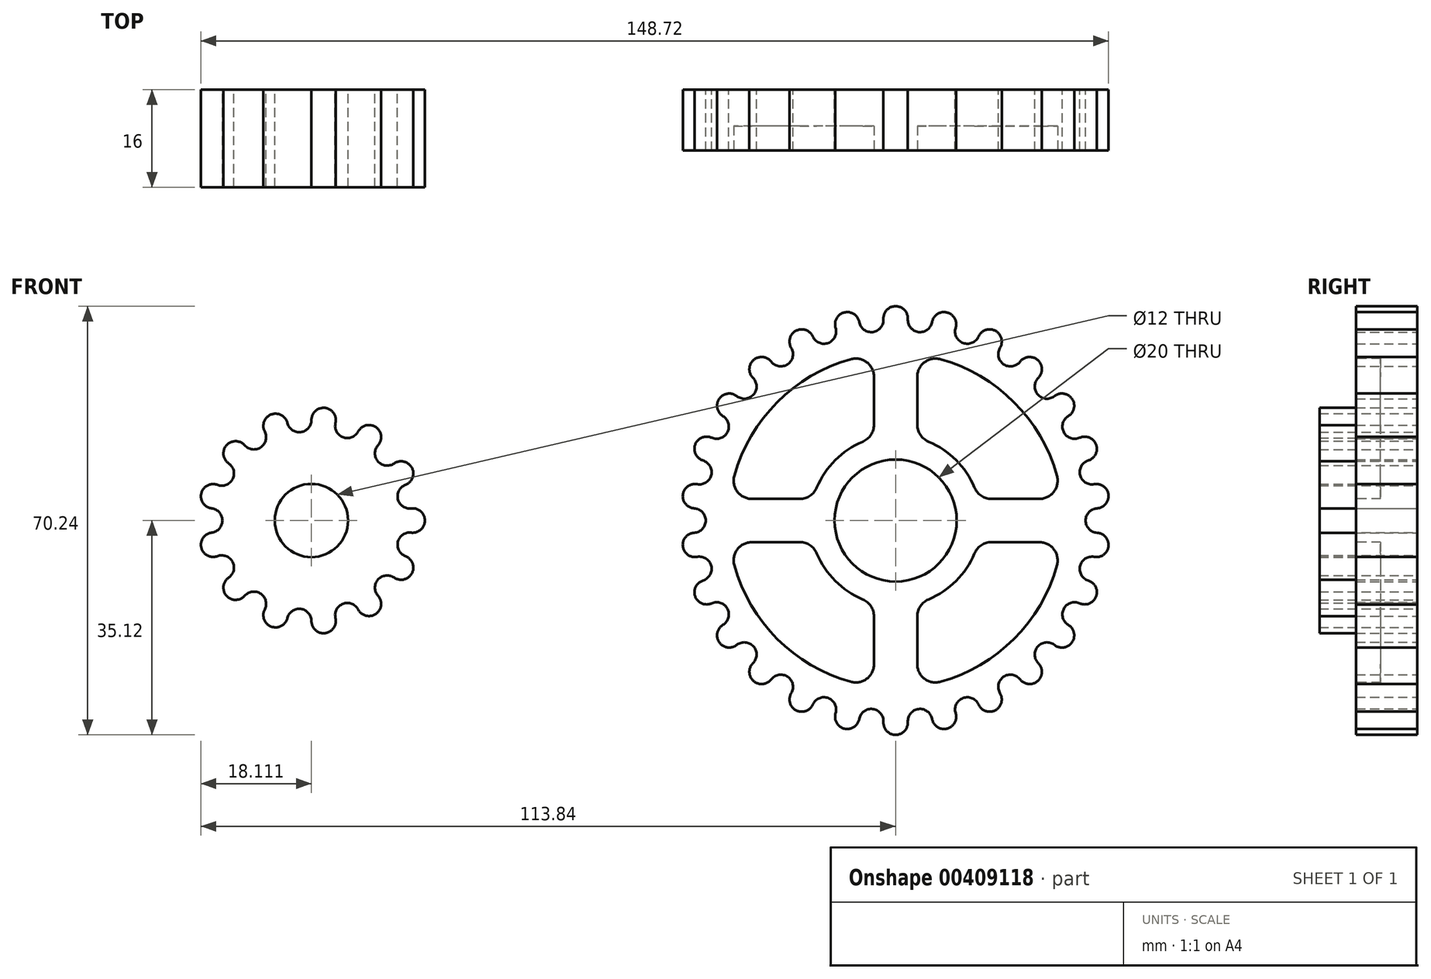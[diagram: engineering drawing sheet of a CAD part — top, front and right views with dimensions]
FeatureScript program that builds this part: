
annotation { "Feature Type Name" : "Feature", "Feature Type Description" : "" }
export const myFeature = defineFeature(function(context is Context, id is Id, definition is map)
    precondition{}
    {
        {
            var Q0;
            Q0=qCreatedBy(makeId("Front.planeOp"),FACE);
            var sketch = newSketch(context, id + "F0", { "sketchPlane" : qUnion([Q0])});
            skLineSegment(sketch, "E0", {"start": v(0, 0) * mm, "end": v(0, 49.58) * mm, "construction": true});
            skArc(sketch, "E1", {"start": v(0, 35.12) * mm, "mid": v(-1.46, 34.5) * mm, "end": v(-2, 33) * mm});
            skArc(sketch, "E2.1.0", {"start": v(-5.96, 32.52) * mm, "mid": v(-3.75, 30.9) * mm, "end": v(-2, 33) * mm});
            skPoint(sketch, "E2.center", {"position": v(0, 0) * mm});
            skLineSegment(sketch, "E3", {"start": v(0, 0) * mm, "end": v(-5.4, 44.45) * mm, "construction": true});
            skArc(sketch, "E4", {"start": v(-5.96, 32.52) * mm, "mid": v(-6.84, 33.84) * mm, "end": v(-8.4, 34.1) * mm});
            skLineSegment(sketch, "E5", {"start": v(0, 0) * mm, "end": v(-10.92, 44.32) * mm, "construction": true});
            skArc(sketch, "E6.1.0", {"start": v(-13.57, 30.15) * mm, "mid": v(-14.74, 31.22) * mm, "end": v(-16.32, 31.1) * mm});
            skArc(sketch, "E6.1.1", {"start": v(-13.57, 30.15) * mm, "mid": v(-11.04, 29.1) * mm, "end": v(-9.84, 31.57) * mm});
            skArc(sketch, "E6.1.2", {"start": v(-8.4, 34.1) * mm, "mid": v(-9.67, 33.14) * mm, "end": v(-9.84, 31.57) * mm});
            skArc(sketch, "E6.2.0", {"start": v(-20.4, 26.03) * mm, "mid": v(-21.78, 26.79) * mm, "end": v(-23.3, 26.3) * mm});
            skArc(sketch, "E6.2.1", {"start": v(-20.4, 26.03) * mm, "mid": v(-17.68, 25.61) * mm, "end": v(-17.1, 28.3) * mm});
            skArc(sketch, "E6.2.2", {"start": v(-16.32, 31.1) * mm, "mid": v(-17.32, 29.87) * mm, "end": v(-17.1, 28.3) * mm});
            skArc(sketch, "E6.3.0", {"start": v(-26.03, 20.4) * mm, "mid": v(-27.56, 20.8) * mm, "end": v(-28.9, 19.95) * mm});
            skArc(sketch, "E6.3.1", {"start": v(-26.03, 20.4) * mm, "mid": v(-23.3, 20.64) * mm, "end": v(-23.38, 23.38) * mm});
            skArc(sketch, "E6.3.2", {"start": v(-23.3, 26.3) * mm, "mid": v(-23.96, 24.85) * mm, "end": v(-23.38, 23.38) * mm});
            skArc(sketch, "E6.4.0", {"start": v(-30.15, 13.57) * mm, "mid": v(-31.74, 13.6) * mm, "end": v(-32.84, 12.46) * mm});
            skArc(sketch, "E6.4.1", {"start": v(-30.15, 13.57) * mm, "mid": v(-27.56, 14.46) * mm, "end": v(-28.3, 17.1) * mm});
            skArc(sketch, "E6.4.2", {"start": v(-28.9, 19.95) * mm, "mid": v(-29.22, 18.4) * mm, "end": v(-28.3, 17.1) * mm});
            skArc(sketch, "E6.5.0", {"start": v(-32.52, 5.96) * mm, "mid": v(-34.07, 5.6) * mm, "end": v(-34.87, 4.23) * mm});
            skArc(sketch, "E6.5.1", {"start": v(-32.52, 5.96) * mm, "mid": v(-30.22, 7.45) * mm, "end": v(-31.57, 9.84) * mm});
            skArc(sketch, "E6.5.2", {"start": v(-32.84, 12.46) * mm, "mid": v(-32.77, 10.87) * mm, "end": v(-31.57, 9.84) * mm});
            skArc(sketch, "E6.6.0", {"start": v(-33, -2) * mm, "mid": v(-34.42, -2.71) * mm, "end": v(-34.87, -4.23) * mm});
            skArc(sketch, "E6.6.1", {"start": v(-33, -2) * mm, "mid": v(-31.12, 0) * mm, "end": v(-33, 2) * mm});
            skArc(sketch, "E6.6.2", {"start": v(-34.87, 4.23) * mm, "mid": v(-34.42, 2.71) * mm, "end": v(-33, 2) * mm});
            skArc(sketch, "E6.7.0", {"start": v(-31.57, -9.84) * mm, "mid": v(-32.77, -10.87) * mm, "end": v(-32.84, -12.46) * mm});
            skArc(sketch, "E6.7.1", {"start": v(-31.57, -9.84) * mm, "mid": v(-30.22, -7.45) * mm, "end": v(-32.52, -5.96) * mm});
            skArc(sketch, "E6.7.2", {"start": v(-34.87, -4.23) * mm, "mid": v(-34.07, -5.6) * mm, "end": v(-32.52, -5.96) * mm});
            skArc(sketch, "E6.8.0", {"start": v(-28.3, -17.1) * mm, "mid": v(-29.22, -18.4) * mm, "end": v(-28.9, -19.95) * mm});
            skArc(sketch, "E6.8.1", {"start": v(-28.3, -17.1) * mm, "mid": v(-27.56, -14.46) * mm, "end": v(-30.15, -13.57) * mm});
            skArc(sketch, "E6.8.2", {"start": v(-32.84, -12.46) * mm, "mid": v(-31.74, -13.6) * mm, "end": v(-30.15, -13.57) * mm});
            skArc(sketch, "E6.9.0", {"start": v(-23.38, -23.38) * mm, "mid": v(-23.96, -24.85) * mm, "end": v(-23.3, -26.3) * mm});
            skArc(sketch, "E6.9.1", {"start": v(-23.38, -23.38) * mm, "mid": v(-23.3, -20.64) * mm, "end": v(-26.03, -20.4) * mm});
            skArc(sketch, "E6.9.2", {"start": v(-28.9, -19.95) * mm, "mid": v(-27.56, -20.8) * mm, "end": v(-26.03, -20.4) * mm});
            skArc(sketch, "E6.10.0", {"start": v(-17.1, -28.3) * mm, "mid": v(-17.32, -29.87) * mm, "end": v(-16.32, -31.1) * mm});
            skArc(sketch, "E6.10.1", {"start": v(-17.1, -28.3) * mm, "mid": v(-17.68, -25.61) * mm, "end": v(-20.4, -26.03) * mm});
            skArc(sketch, "E6.10.2", {"start": v(-23.3, -26.3) * mm, "mid": v(-21.78, -26.79) * mm, "end": v(-20.4, -26.03) * mm});
            skArc(sketch, "E6.11.0", {"start": v(-9.84, -31.57) * mm, "mid": v(-9.67, -33.14) * mm, "end": v(-8.4, -34.1) * mm});
            skArc(sketch, "E6.11.1", {"start": v(-9.84, -31.57) * mm, "mid": v(-11.04, -29.1) * mm, "end": v(-13.57, -30.15) * mm});
            skArc(sketch, "E6.11.2", {"start": v(-16.32, -31.1) * mm, "mid": v(-14.74, -31.22) * mm, "end": v(-13.57, -30.15) * mm});
            skArc(sketch, "E6.12.0", {"start": v(-2, -33) * mm, "mid": v(-1.46, -34.5) * mm, "end": v(0, -35.12) * mm});
            skArc(sketch, "E6.12.1", {"start": v(-2, -33) * mm, "mid": v(-3.75, -30.9) * mm, "end": v(-5.96, -32.52) * mm});
            skArc(sketch, "E6.12.2", {"start": v(-8.4, -34.1) * mm, "mid": v(-6.84, -33.84) * mm, "end": v(-5.96, -32.52) * mm});
            skArc(sketch, "E6.13.0", {"start": v(5.96, -32.52) * mm, "mid": v(6.84, -33.84) * mm, "end": v(8.4, -34.1) * mm});
            skArc(sketch, "E6.13.1", {"start": v(5.96, -32.52) * mm, "mid": v(3.75, -30.9) * mm, "end": v(2, -33) * mm});
            skArc(sketch, "E6.13.2", {"start": v(0, -35.12) * mm, "mid": v(1.46, -34.5) * mm, "end": v(2, -33) * mm});
            skArc(sketch, "E6.14.0", {"start": v(13.57, -30.15) * mm, "mid": v(14.74, -31.22) * mm, "end": v(16.32, -31.1) * mm});
            skArc(sketch, "E6.14.1", {"start": v(13.57, -30.15) * mm, "mid": v(11.04, -29.1) * mm, "end": v(9.84, -31.57) * mm});
            skArc(sketch, "E6.14.2", {"start": v(8.4, -34.1) * mm, "mid": v(9.67, -33.14) * mm, "end": v(9.84, -31.57) * mm});
            skArc(sketch, "E6.15.0", {"start": v(20.4, -26.03) * mm, "mid": v(21.78, -26.79) * mm, "end": v(23.3, -26.3) * mm});
            skArc(sketch, "E6.15.1", {"start": v(20.4, -26.03) * mm, "mid": v(17.68, -25.61) * mm, "end": v(17.1, -28.3) * mm});
            skArc(sketch, "E6.15.2", {"start": v(16.32, -31.1) * mm, "mid": v(17.32, -29.87) * mm, "end": v(17.1, -28.3) * mm});
            skArc(sketch, "E6.16.0", {"start": v(26.03, -20.4) * mm, "mid": v(27.56, -20.8) * mm, "end": v(28.9, -19.95) * mm});
            skArc(sketch, "E6.16.1", {"start": v(26.03, -20.4) * mm, "mid": v(23.3, -20.64) * mm, "end": v(23.38, -23.38) * mm});
            skArc(sketch, "E6.16.2", {"start": v(23.3, -26.3) * mm, "mid": v(23.96, -24.85) * mm, "end": v(23.38, -23.38) * mm});
            skArc(sketch, "E6.17.0", {"start": v(30.15, -13.57) * mm, "mid": v(31.74, -13.6) * mm, "end": v(32.84, -12.46) * mm});
            skArc(sketch, "E6.17.1", {"start": v(30.15, -13.57) * mm, "mid": v(27.56, -14.46) * mm, "end": v(28.3, -17.1) * mm});
            skArc(sketch, "E6.17.2", {"start": v(28.9, -19.95) * mm, "mid": v(29.22, -18.4) * mm, "end": v(28.3, -17.1) * mm});
            skArc(sketch, "E6.18.0", {"start": v(32.52, -5.96) * mm, "mid": v(34.07, -5.6) * mm, "end": v(34.87, -4.23) * mm});
            skArc(sketch, "E6.18.1", {"start": v(32.52, -5.96) * mm, "mid": v(30.22, -7.45) * mm, "end": v(31.57, -9.84) * mm});
            skArc(sketch, "E6.18.2", {"start": v(32.84, -12.46) * mm, "mid": v(32.77, -10.87) * mm, "end": v(31.57, -9.84) * mm});
            skArc(sketch, "E6.19.0", {"start": v(33, 2) * mm, "mid": v(34.42, 2.71) * mm, "end": v(34.87, 4.23) * mm});
            skArc(sketch, "E6.19.1", {"start": v(33, 2) * mm, "mid": v(31.12, 0) * mm, "end": v(33, -2) * mm});
            skArc(sketch, "E6.19.2", {"start": v(34.87, -4.23) * mm, "mid": v(34.42, -2.71) * mm, "end": v(33, -2) * mm});
            skArc(sketch, "E6.20.0", {"start": v(31.57, 9.84) * mm, "mid": v(32.77, 10.87) * mm, "end": v(32.84, 12.46) * mm});
            skArc(sketch, "E6.20.1", {"start": v(31.57, 9.84) * mm, "mid": v(30.22, 7.45) * mm, "end": v(32.52, 5.96) * mm});
            skArc(sketch, "E6.20.2", {"start": v(34.87, 4.23) * mm, "mid": v(34.07, 5.6) * mm, "end": v(32.52, 5.96) * mm});
            skArc(sketch, "E6.21.0", {"start": v(28.3, 17.1) * mm, "mid": v(29.22, 18.4) * mm, "end": v(28.9, 19.95) * mm});
            skArc(sketch, "E6.21.1", {"start": v(28.3, 17.1) * mm, "mid": v(27.56, 14.46) * mm, "end": v(30.15, 13.57) * mm});
            skArc(sketch, "E6.21.2", {"start": v(32.84, 12.46) * mm, "mid": v(31.74, 13.6) * mm, "end": v(30.15, 13.57) * mm});
            skArc(sketch, "E6.22.0", {"start": v(23.38, 23.38) * mm, "mid": v(23.96, 24.85) * mm, "end": v(23.3, 26.3) * mm});
            skArc(sketch, "E6.22.1", {"start": v(23.38, 23.38) * mm, "mid": v(23.3, 20.64) * mm, "end": v(26.03, 20.4) * mm});
            skArc(sketch, "E6.22.2", {"start": v(28.9, 19.95) * mm, "mid": v(27.56, 20.8) * mm, "end": v(26.03, 20.4) * mm});
            skArc(sketch, "E6.23.0", {"start": v(17.1, 28.3) * mm, "mid": v(17.32, 29.87) * mm, "end": v(16.32, 31.1) * mm});
            skArc(sketch, "E6.23.1", {"start": v(17.1, 28.3) * mm, "mid": v(17.68, 25.61) * mm, "end": v(20.4, 26.03) * mm});
            skArc(sketch, "E6.23.2", {"start": v(23.3, 26.3) * mm, "mid": v(21.78, 26.79) * mm, "end": v(20.4, 26.03) * mm});
            skArc(sketch, "E6.24.0", {"start": v(9.84, 31.57) * mm, "mid": v(9.67, 33.14) * mm, "end": v(8.4, 34.1) * mm});
            skArc(sketch, "E6.24.1", {"start": v(9.84, 31.57) * mm, "mid": v(11.04, 29.1) * mm, "end": v(13.57, 30.15) * mm});
            skArc(sketch, "E6.24.2", {"start": v(16.32, 31.1) * mm, "mid": v(14.74, 31.22) * mm, "end": v(13.57, 30.15) * mm});
            skArc(sketch, "E6.25.0", {"start": v(2, 33) * mm, "mid": v(1.46, 34.5) * mm, "end": v(0, 35.12) * mm});
            skArc(sketch, "E6.25.1", {"start": v(2, 33) * mm, "mid": v(3.75, 30.9) * mm, "end": v(5.96, 32.52) * mm});
            skArc(sketch, "E6.25.2", {"start": v(8.4, 34.1) * mm, "mid": v(6.84, 33.84) * mm, "end": v(5.96, 32.52) * mm});
            skCircle(sketch, "E7", {"center": v(0, 0) * mm, "radius": 10 * mm});
            skLineSegment(sketch, "E8", {"start": v(-95.73, 0) * mm, "end": v(-52.5, 0) * mm, "construction": true});
            skArc(sketch, "E9", {"start": v(-79.38, -1.99) * mm, "mid": v(-77.14, 0) * mm, "end": v(-79.38, 1.99) * mm});
            skArc(sketch, "E10.1.0", {"start": v(-81.56, 3.5) * mm, "mid": v(-80.75, 2.32) * mm, "end": v(-79.38, 1.99) * mm});
            skArc(sketch, "E10.25.0", {"start": v(-79.38, -1.99) * mm, "mid": v(-80.75, -2.32) * mm, "end": v(-81.56, -3.5) * mm});
            skPoint(sketch, "E10.center", {"position": v(-95.73, 0) * mm});
            skLineSegment(sketch, "E11", {"start": v(-95.73, 0) * mm, "end": v(-68.7, 6.66) * mm, "construction": true});
            skLineSegment(sketch, "E12", {"start": v(-95.73, 0) * mm, "end": v(-75.32, -5.03) * mm, "construction": true});
            skArc(sketch, "E13.1.0", {"start": v(-84.8, 9.68) * mm, "mid": v(-83.55, 9.02) * mm, "end": v(-82.17, 9.36) * mm});
            skArc(sketch, "E13.1.1", {"start": v(-80.33, 5.84) * mm, "mid": v(-79.27, 8.64) * mm, "end": v(-82.17, 9.36) * mm});
            skArc(sketch, "E13.1.2", {"start": v(-80.33, 5.84) * mm, "mid": v(-81.39, 4.9) * mm, "end": v(-81.56, 3.5) * mm});
            skArc(sketch, "E13.2.0", {"start": v(-90.55, 13.64) * mm, "mid": v(-89.14, 13.64) * mm, "end": v(-88.07, 14.58) * mm});
            skArc(sketch, "E13.2.1", {"start": v(-84.8, 12.33) * mm, "mid": v(-85.17, 15.3) * mm, "end": v(-88.07, 14.58) * mm});
            skArc(sketch, "E13.2.2", {"start": v(-84.8, 12.33) * mm, "mid": v(-85.3, 11) * mm, "end": v(-84.8, 9.68) * mm});
            skArc(sketch, "E14.2.3.0", {"start": v(-97.49, 14.49) * mm, "mid": v(-96.23, 15.15) * mm, "end": v(-95.73, 16.47) * mm});
            skArc(sketch, "E14.4.3.0", {"start": v(-91.79, 16) * mm, "mid": v(-93.49, 18.46) * mm, "end": v(-95.73, 16.47) * mm});
            skArc(sketch, "E14.8.3.0", {"start": v(-91.79, 16) * mm, "mid": v(-91.62, 14.58) * mm, "end": v(-90.55, 13.64) * mm});
            skArc(sketch, "E14.2.4.0", {"start": v(-104.02, 12) * mm, "mid": v(-103.21, 13.18) * mm, "end": v(-103.38, 14.58) * mm});
            skArc(sketch, "E14.4.4.0", {"start": v(-99.67, 16) * mm, "mid": v(-102.32, 17.38) * mm, "end": v(-103.38, 14.58) * mm});
            skArc(sketch, "E14.8.4.0", {"start": v(-99.67, 16) * mm, "mid": v(-98.86, 14.83) * mm, "end": v(-97.49, 14.49) * mm});
            skArc(sketch, "E14.2.5.0", {"start": v(-108.65, 6.78) * mm, "mid": v(-108.48, 8.19) * mm, "end": v(-109.28, 9.36) * mm});
            skArc(sketch, "E14.4.5.0", {"start": v(-106.65, 12.33) * mm, "mid": v(-109.65, 12.33) * mm, "end": v(-109.28, 9.36) * mm});
            skArc(sketch, "E14.8.5.0", {"start": v(-106.65, 12.33) * mm, "mid": v(-105.4, 11.67) * mm, "end": v(-104.02, 12) * mm});
            skArc(sketch, "E14.2.6.0", {"start": v(-110.32, 0) * mm, "mid": v(-110.82, 1.33) * mm, "end": v(-112.08, 1.99) * mm});
            skArc(sketch, "E14.4.6.0", {"start": v(-111.13, 5.84) * mm, "mid": v(-113.78, 4.45) * mm, "end": v(-112.08, 1.99) * mm});
            skArc(sketch, "E14.8.6.0", {"start": v(-111.13, 5.84) * mm, "mid": v(-109.71, 5.84) * mm, "end": v(-108.65, 6.78) * mm});
            skArc(sketch, "E14.2.7.0", {"start": v(-108.65, -6.78) * mm, "mid": v(-109.71, -5.84) * mm, "end": v(-111.13, -5.84) * mm});
            skArc(sketch, "E14.4.7.0", {"start": v(-112.08, -1.99) * mm, "mid": v(-113.78, -4.45) * mm, "end": v(-111.13, -5.84) * mm});
            skArc(sketch, "E14.8.7.0", {"start": v(-112.08, -1.99) * mm, "mid": v(-110.82, -1.33) * mm, "end": v(-110.32, 0) * mm});
            skArc(sketch, "E14.2.8.0", {"start": v(-104.02, -12) * mm, "mid": v(-105.4, -11.67) * mm, "end": v(-106.65, -12.33) * mm});
            skArc(sketch, "E14.4.8.0", {"start": v(-109.28, -9.36) * mm, "mid": v(-109.65, -12.33) * mm, "end": v(-106.65, -12.33) * mm});
            skArc(sketch, "E14.8.8.0", {"start": v(-109.28, -9.36) * mm, "mid": v(-108.48, -8.19) * mm, "end": v(-108.65, -6.78) * mm});
            skArc(sketch, "E14.2.9.0", {"start": v(-97.49, -14.49) * mm, "mid": v(-98.86, -14.83) * mm, "end": v(-99.67, -16) * mm});
            skArc(sketch, "E14.4.9.0", {"start": v(-103.38, -14.58) * mm, "mid": v(-102.32, -17.38) * mm, "end": v(-99.67, -16) * mm});
            skArc(sketch, "E14.8.9.0", {"start": v(-103.38, -14.58) * mm, "mid": v(-103.21, -13.18) * mm, "end": v(-104.02, -12) * mm});
            skArc(sketch, "E14.2.10.0", {"start": v(-90.55, -13.64) * mm, "mid": v(-91.62, -14.58) * mm, "end": v(-91.79, -16) * mm});
            skArc(sketch, "E14.4.10.0", {"start": v(-95.73, -16.47) * mm, "mid": v(-93.49, -18.46) * mm, "end": v(-91.79, -16) * mm});
            skArc(sketch, "E14.8.10.0", {"start": v(-95.73, -16.47) * mm, "mid": v(-96.23, -15.15) * mm, "end": v(-97.49, -14.49) * mm});
            skArc(sketch, "E14.2.11.0", {"start": v(-84.8, -9.68) * mm, "mid": v(-85.3, -11) * mm, "end": v(-84.8, -12.33) * mm});
            skArc(sketch, "E14.4.11.0", {"start": v(-88.07, -14.58) * mm, "mid": v(-85.17, -15.3) * mm, "end": v(-84.8, -12.33) * mm});
            skArc(sketch, "E14.8.11.0", {"start": v(-88.07, -14.58) * mm, "mid": v(-89.14, -13.64) * mm, "end": v(-90.55, -13.64) * mm});
            skArc(sketch, "E14.2.12.0", {"start": v(-81.56, -3.5) * mm, "mid": v(-81.39, -4.9) * mm, "end": v(-80.33, -5.84) * mm});
            skArc(sketch, "E14.4.12.0", {"start": v(-82.17, -9.36) * mm, "mid": v(-79.27, -8.64) * mm, "end": v(-80.33, -5.84) * mm});
            skArc(sketch, "E14.8.12.0", {"start": v(-82.17, -9.36) * mm, "mid": v(-83.55, -9.02) * mm, "end": v(-84.8, -9.68) * mm});
            skCircle(sketch, "E15", {"center": v(-95.73, 0) * mm, "radius": 6 * mm});
            skSolve(sketch);
        }
        {
            var Q0;
            Q0=makeQuery(id+"F0.imprint","IMPRINT",FACE,{"disambiguationData":[TD([[makeQuery(id+"F0.imprint","IMPRINT",EDGE,{"derivedFrom":sQuery(id+"F0.wireOp",EDGE,"E1")}),1.0]])]});
            extrude(context, id + "F1", {"entities" : qUnion([Q0]), "depth" : 10 * mm});
        }
        {
            var Q0;
            Q0=makeQuery(id+"F0.imprint","IMPRINT",FACE,{"disambiguationData":[TD([[makeQuery(id+"F0.imprint","IMPRINT",EDGE,{"derivedFrom":sQuery(id+"F0.wireOp",EDGE,"E9")}),1.0]])]});
            extrude(context, id + "F2", {"entities" : qUnion([Q0]), "depth" : 16 * mm});
        }
        {
            var Q0;
            Q0=makeQuery(id+"F1.opExtrude","CAP_FACE",FACE,{"disambiguationData":[OSD([sQuery(id+"F0.wireOp",EDGE,"E1"),sQuery(id+"F0.wireOp",EDGE,"E2.1.0"),sQuery(id+"F0.wireOp",EDGE,"E4"),sQuery(id+"F0.wireOp",EDGE,"E6.1.0"),sQuery(id+"F0.wireOp",EDGE,"E6.1.1"),sQuery(id+"F0.wireOp",EDGE,"E6.1.2"),sQuery(id+"F0.wireOp",EDGE,"E6.2.0"),sQuery(id+"F0.wireOp",EDGE,"E6.2.1"),sQuery(id+"F0.wireOp",EDGE,"E6.2.2"),sQuery(id+"F0.wireOp",EDGE,"E6.3.0"),sQuery(id+"F0.wireOp",EDGE,"E6.3.1"),sQuery(id+"F0.wireOp",EDGE,"E6.3.2"),sQuery(id+"F0.wireOp",EDGE,"E6.4.0"),sQuery(id+"F0.wireOp",EDGE,"E6.4.1"),sQuery(id+"F0.wireOp",EDGE,"E6.4.2"),sQuery(id+"F0.wireOp",EDGE,"E6.5.0"),sQuery(id+"F0.wireOp",EDGE,"E6.5.1"),sQuery(id+"F0.wireOp",EDGE,"E6.5.2"),sQuery(id+"F0.wireOp",EDGE,"E6.6.0"),sQuery(id+"F0.wireOp",EDGE,"E6.6.1"),sQuery(id+"F0.wireOp",EDGE,"E6.6.2"),sQuery(id+"F0.wireOp",EDGE,"E6.7.0"),sQuery(id+"F0.wireOp",EDGE,"E6.7.1"),sQuery(id+"F0.wireOp",EDGE,"E6.7.2"),sQuery(id+"F0.wireOp",EDGE,"E6.8.0"),sQuery(id+"F0.wireOp",EDGE,"E6.8.1"),sQuery(id+"F0.wireOp",EDGE,"E6.8.2"),sQuery(id+"F0.wireOp",EDGE,"E6.9.0"),sQuery(id+"F0.wireOp",EDGE,"E6.9.1"),sQuery(id+"F0.wireOp",EDGE,"E6.9.2"),sQuery(id+"F0.wireOp",EDGE,"E6.10.0"),sQuery(id+"F0.wireOp",EDGE,"E6.10.1"),sQuery(id+"F0.wireOp",EDGE,"E6.10.2"),sQuery(id+"F0.wireOp",EDGE,"E6.11.0"),sQuery(id+"F0.wireOp",EDGE,"E6.11.1"),sQuery(id+"F0.wireOp",EDGE,"E6.11.2"),sQuery(id+"F0.wireOp",EDGE,"E6.12.0"),sQuery(id+"F0.wireOp",EDGE,"E6.12.1"),sQuery(id+"F0.wireOp",EDGE,"E6.12.2"),sQuery(id+"F0.wireOp",EDGE,"E6.13.0"),sQuery(id+"F0.wireOp",EDGE,"E6.13.1"),sQuery(id+"F0.wireOp",EDGE,"E6.13.2"),sQuery(id+"F0.wireOp",EDGE,"E6.14.0"),sQuery(id+"F0.wireOp",EDGE,"E6.14.1"),sQuery(id+"F0.wireOp",EDGE,"E6.14.2"),sQuery(id+"F0.wireOp",EDGE,"E6.15.0"),sQuery(id+"F0.wireOp",EDGE,"E6.15.1"),sQuery(id+"F0.wireOp",EDGE,"E6.15.2"),sQuery(id+"F0.wireOp",EDGE,"E6.16.0"),sQuery(id+"F0.wireOp",EDGE,"E6.16.1"),sQuery(id+"F0.wireOp",EDGE,"E6.16.2"),sQuery(id+"F0.wireOp",EDGE,"E6.17.0"),sQuery(id+"F0.wireOp",EDGE,"E6.17.1"),sQuery(id+"F0.wireOp",EDGE,"E6.17.2"),sQuery(id+"F0.wireOp",EDGE,"E6.18.0"),sQuery(id+"F0.wireOp",EDGE,"E6.18.1"),sQuery(id+"F0.wireOp",EDGE,"E6.18.2"),sQuery(id+"F0.wireOp",EDGE,"E6.19.0"),sQuery(id+"F0.wireOp",EDGE,"E6.19.1"),sQuery(id+"F0.wireOp",EDGE,"E6.19.2"),sQuery(id+"F0.wireOp",EDGE,"E6.20.0"),sQuery(id+"F0.wireOp",EDGE,"E6.20.1"),sQuery(id+"F0.wireOp",EDGE,"E6.20.2"),sQuery(id+"F0.wireOp",EDGE,"E6.21.0"),sQuery(id+"F0.wireOp",EDGE,"E6.21.1"),sQuery(id+"F0.wireOp",EDGE,"E6.21.2"),sQuery(id+"F0.wireOp",EDGE,"E6.22.0"),sQuery(id+"F0.wireOp",EDGE,"E6.22.1"),sQuery(id+"F0.wireOp",EDGE,"E6.22.2"),sQuery(id+"F0.wireOp",EDGE,"E6.23.0"),sQuery(id+"F0.wireOp",EDGE,"E6.23.1"),sQuery(id+"F0.wireOp",EDGE,"E6.23.2"),sQuery(id+"F0.wireOp",EDGE,"E6.24.0"),sQuery(id+"F0.wireOp",EDGE,"E6.24.1"),sQuery(id+"F0.wireOp",EDGE,"E6.24.2"),sQuery(id+"F0.wireOp",EDGE,"E6.25.0"),sQuery(id+"F0.wireOp",EDGE,"E6.25.1"),sQuery(id+"F0.wireOp",EDGE,"E6.25.2"),sQuery(id+"F0.wireOp",EDGE,"E7")])],"isStart":false});
            var sketch = newSketch(context, id + "F3", { "sketchPlane" : qUnion([Q0])});
            skLineSegment(sketch, "E16", {"start": v(0, 0) * mm, "end": v(34.06, 34.06) * mm, "construction": true});
            skLineSegment(sketch, "E17", {"start": v(3.54, 15.69) * mm, "end": v(3.54, 23.54) * mm});
            skLineSegment(sketch, "E18", {"start": v(15.69, 3.54) * mm, "end": v(23.54, 3.54) * mm});
            skArc(sketch, "E19", {"start": v(7.35, 26.43) * mm, "mid": v(19.4, 19.4) * mm, "end": v(26.43, 7.35) * mm});
            skPoint(sketch, "E20.visualSharp", {"position": v(3.54, 27.2) * mm});
            skArc(sketch, "E20.filletArc", {"start": v(7.35, 26.43) * mm, "mid": v(4.73, 25.93) * mm, "end": v(3.54, 23.54) * mm});
            skPoint(sketch, "E21.visualSharp", {"position": v(27.2, 3.54) * mm});
            skArc(sketch, "E21.filletArc", {"start": v(23.54, 3.54) * mm, "mid": v(25.93, 4.73) * mm, "end": v(26.43, 7.35) * mm});
            skArc(sketch, "E22", {"start": v(12.92, 5.39) * mm, "mid": v(9.9, 9.9) * mm, "end": v(5.39, 12.92) * mm});
            skPoint(sketch, "E23.orphan", {"position": v(3.54, 3.54) * mm});
            skPoint(sketch, "E24.visualSharp", {"position": v(3.54, 13.54) * mm});
            skArc(sketch, "E24.filletArc", {"start": v(3.54, 15.69) * mm, "mid": v(4.05, 14.03) * mm, "end": v(5.39, 12.92) * mm});
            skPoint(sketch, "E25.visualSharp", {"position": v(13.54, 3.54) * mm});
            skArc(sketch, "E25.filletArc", {"start": v(12.92, 5.39) * mm, "mid": v(14.03, 4.05) * mm, "end": v(15.69, 3.54) * mm});
            skArc(sketch, "E26.1.0", {"start": v(-26.43, 7.35) * mm, "mid": v(-19.4, 19.4) * mm, "end": v(-7.35, 26.43) * mm});
            skArc(sketch, "E26.1.1", {"start": v(-3.54, 23.54) * mm, "mid": v(-4.73, 25.93) * mm, "end": v(-7.35, 26.43) * mm});
            skLineSegment(sketch, "E26.1.2", {"start": v(-3.54, 15.69) * mm, "end": v(-3.54, 23.54) * mm});
            skArc(sketch, "E26.1.3", {"start": v(-5.39, 12.92) * mm, "mid": v(-4.05, 14.03) * mm, "end": v(-3.54, 15.69) * mm});
            skArc(sketch, "E26.1.4", {"start": v(-5.39, 12.92) * mm, "mid": v(-9.9, 9.9) * mm, "end": v(-12.92, 5.39) * mm});
            skArc(sketch, "E26.1.5", {"start": v(-15.69, 3.54) * mm, "mid": v(-14.03, 4.05) * mm, "end": v(-12.92, 5.39) * mm});
            skLineSegment(sketch, "E26.1.6", {"start": v(-15.69, 3.54) * mm, "end": v(-23.54, 3.54) * mm});
            skArc(sketch, "E26.1.7", {"start": v(-26.43, 7.35) * mm, "mid": v(-25.93, 4.73) * mm, "end": v(-23.54, 3.54) * mm});
            skArc(sketch, "E26.2.0", {"start": v(-7.35, -26.43) * mm, "mid": v(-19.4, -19.4) * mm, "end": v(-26.43, -7.35) * mm});
            skArc(sketch, "E26.2.1", {"start": v(-23.54, -3.54) * mm, "mid": v(-25.93, -4.73) * mm, "end": v(-26.43, -7.35) * mm});
            skLineSegment(sketch, "E26.2.2", {"start": v(-15.69, -3.54) * mm, "end": v(-23.54, -3.54) * mm});
            skArc(sketch, "E26.2.3", {"start": v(-12.92, -5.39) * mm, "mid": v(-14.03, -4.05) * mm, "end": v(-15.69, -3.54) * mm});
            skArc(sketch, "E26.2.4", {"start": v(-12.92, -5.39) * mm, "mid": v(-9.9, -9.9) * mm, "end": v(-5.39, -12.92) * mm});
            skArc(sketch, "E26.2.5", {"start": v(-3.54, -15.69) * mm, "mid": v(-4.05, -14.03) * mm, "end": v(-5.39, -12.92) * mm});
            skLineSegment(sketch, "E26.2.6", {"start": v(-3.54, -15.69) * mm, "end": v(-3.54, -23.54) * mm});
            skArc(sketch, "E26.2.7", {"start": v(-7.35, -26.43) * mm, "mid": v(-4.73, -25.93) * mm, "end": v(-3.54, -23.54) * mm});
            skArc(sketch, "E26.3.0", {"start": v(26.43, -7.35) * mm, "mid": v(19.4, -19.4) * mm, "end": v(7.35, -26.43) * mm});
            skArc(sketch, "E26.3.1", {"start": v(3.54, -23.54) * mm, "mid": v(4.73, -25.93) * mm, "end": v(7.35, -26.43) * mm});
            skLineSegment(sketch, "E26.3.2", {"start": v(3.54, -15.69) * mm, "end": v(3.54, -23.54) * mm});
            skArc(sketch, "E26.3.3", {"start": v(5.39, -12.92) * mm, "mid": v(4.05, -14.03) * mm, "end": v(3.54, -15.69) * mm});
            skArc(sketch, "E26.3.4", {"start": v(5.39, -12.92) * mm, "mid": v(9.9, -9.9) * mm, "end": v(12.92, -5.39) * mm});
            skArc(sketch, "E26.3.5", {"start": v(15.69, -3.54) * mm, "mid": v(14.03, -4.05) * mm, "end": v(12.92, -5.39) * mm});
            skLineSegment(sketch, "E26.3.6", {"start": v(15.69, -3.54) * mm, "end": v(23.54, -3.54) * mm});
            skArc(sketch, "E26.3.7", {"start": v(26.43, -7.35) * mm, "mid": v(25.93, -4.73) * mm, "end": v(23.54, -3.54) * mm});
            skSolve(sketch);
        }
        {
            var Q0;
            Q0 = qSketchRegion(id + "F3", true);
            extrude(context, id + "F4", {"entities" : qUnion([Q0]), "operationType" : NewBodyOperationType.REMOVE, "oppositeDirection" : true, "depth" : 4 * mm});
        }
    });
